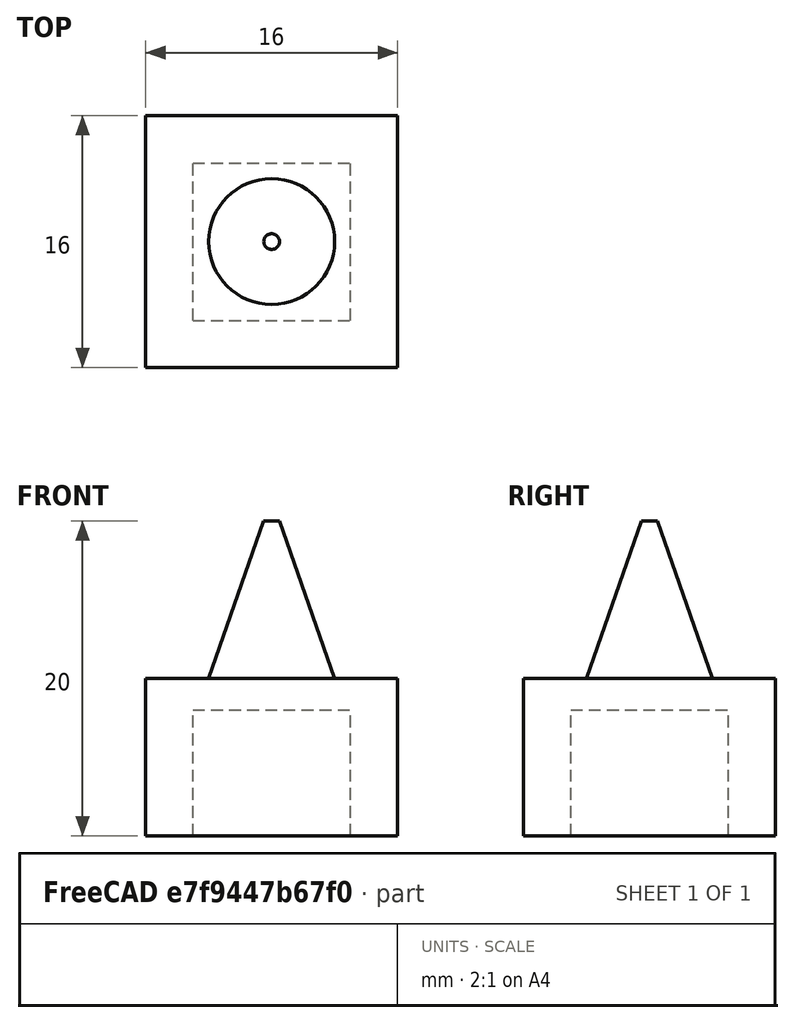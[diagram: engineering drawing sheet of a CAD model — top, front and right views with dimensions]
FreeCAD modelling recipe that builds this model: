
FCSTD DOCUMENT  (FreeCAD 0.18.3R)
Label: cone
License: All rights reserved
LicenseURL: http://en.wikipedia.org/wiki/All_rights_reserved
objects: Part::Box×2, Part::Cone×1, Part::Fuse×1, Part::Cut×1
note: 5 computed .brp shape members not serialized (recipe doc carries the construction recipe); baked Part::Feature solids carry a one-line shape summary decoded from their .brp

FEATURE [Part::Box] Box  label="Cube"
  AttacherType = Attacher::AttachEngine3D
  Height = 10
  Length = 16
  Placement = pos=(-8,-8,0) rot=(0,0,1;0rad)
  Width = 16
FEATURE [Part::Cone] Cone
  Angle = 360
  AttacherType = Attacher::AttachEngine3D
  Height = 10
  Placement = pos=(0,0,20) rot=(0,1,0;3.14159rad)
  Radius1 = 0.5
  Radius2 = 4
FEATURE [Part::Fuse] Fusion
  Base = -> Box
  Tool = -> Cone
FEATURE [Part::Box] Box001  label="Cube001"
  AttacherType = Attacher::AttachEngine3D
  Height = 8
  Length = 10
  Placement = pos=(-5,-5,0) rot=(0,0,1;0rad)
  Width = 10
FEATURE [Part::Cut] Cut
  Base = -> Fusion
  Tool = -> Box001
